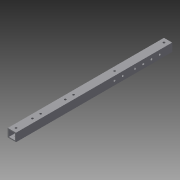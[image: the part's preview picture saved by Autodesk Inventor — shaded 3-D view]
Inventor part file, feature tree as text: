
AUTODESK INVENTOR PART (.ipt)
format: ipt  version: 2015 SP1 (Build 190203100, 203)  size: 174,592 bytes
history: native  units: in
note: dims shown in document units (in); Inventor stores cm internally (conversion verified against a paired STEP export)
features: sketch x7, hole x5, projected_geometry x3, extrude x2
ambient origin geometry x8: Origin, YZ Plane, XZ Plane, XY Plane, X Axis, Y Axis, Z Axis, Center Point
bodies: Solid1 (feature_tree)
feature tree (17):
  extrude  "Extrusion1"  Depth=1.0in
  sketch  "Sketch2"  dims[d2=0.75in d3=0.75in]
  hole  "Hole2"  [1 undecoded]
  hole  "Hole3"  [1 undecoded]
  hole  "Hole4"  [1 undecoded]
  extrude  "Extrusion2"  Depth=0.5in
  hole  "Hole6"  [1 undecoded]
  hole  "Hole7"  [1 undecoded]
  sketch  "Sketch1"  dims[d0=1.0in d1=1.0in]
  projected_geometry  "Projected Loop1"
  sketch  "Sketch3"  dims[d4=0.125in d5=0.125in]
  sketch  "Sketch4"  dims[d6=12.0in d7=0.0in d8=0.5in]
  projected_geometry  "Projected Loop2"
  sketch  "Sketch5"  dims[d9=0.5in d10=0.5in]
  sketch  "Sketch6"  dims[d11=0.5in d19=0.5in]
  sketch  "Sketch7"  dims[d20=0.5in d21=0.5in d22=1.5in d23=3.5in d24=2.5in d25=0.25in d26=0.75in d27=0.375in d28=0.25in d29=0.5635in d30=1.0in d31=0.8108in d32=0.5in d33=5.5in d34=0.25in d35=0.75in d36=0.375in d37=0.25in d38=0.5635in d39=1.0in d40=0.8108in d41=5.0in d42=7.5in d43=6.0in d44=0.5in d45=0.5in d46=0.5in d47=0.25in d48=0.75in d49=0.375in d50=0.25in d51=0.5635in d52=1.0in d53=0.8108in d54=7.0in d55=0.0in d56=0.5in d57=0.5in d65=2.5in d66=0.5in d67=0.25in d68=0.75in d69=0.375in d70=0.25in d71=0.5635in d72=1.0in d73=0.8108in d74=0.5in d75=0.5in d76=3.5in d77=6.5in d78=0.25in d79=0.75in d80=0.375in d81=0.25in d82=0.5635in d83=1.0in d84=0.8108in]
  projected_geometry  "Projected Loop3"
note: 5 required parameter values undecoded (feature->parameter linkage not recoverable at this tier; creation-order binding heuristic only, values carry confidence <= 0.55)
